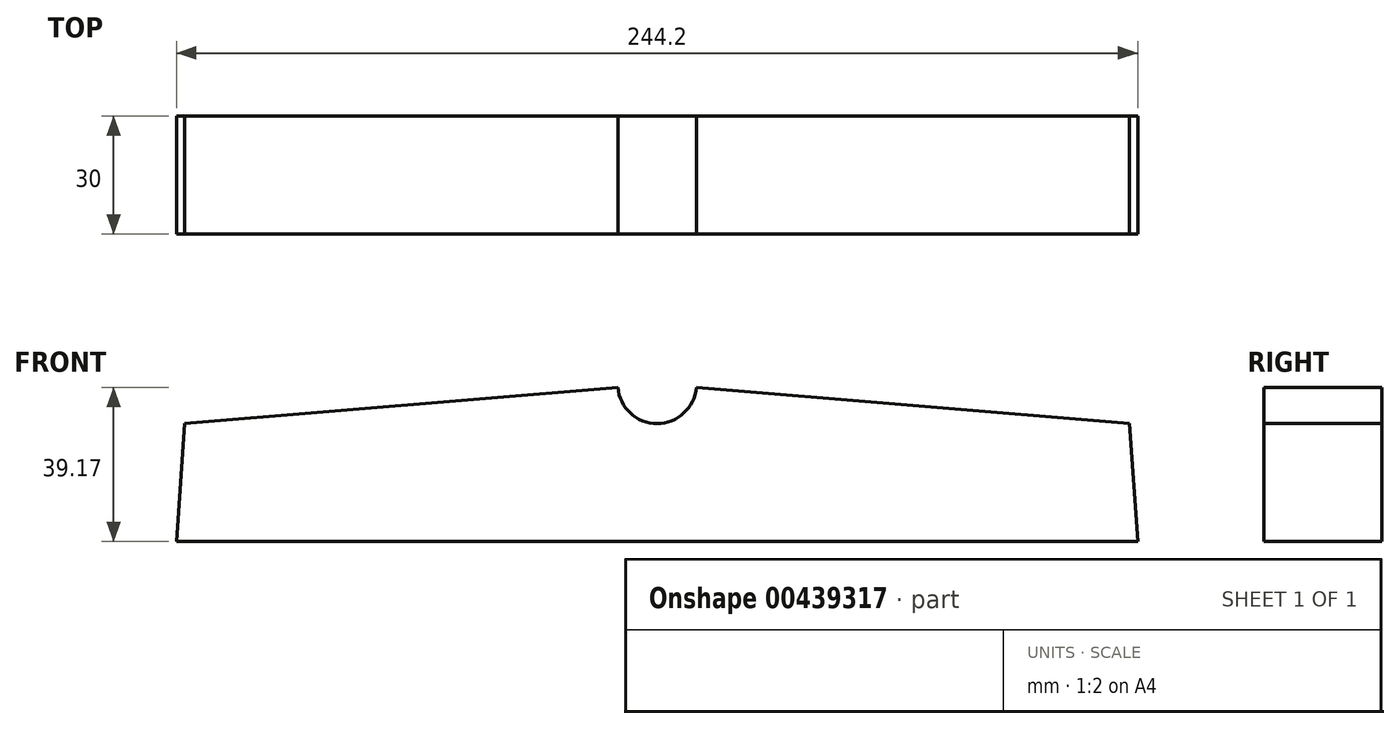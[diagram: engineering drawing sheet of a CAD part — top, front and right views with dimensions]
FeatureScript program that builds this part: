
annotation { "Feature Type Name" : "Feature", "Feature Type Description" : "" }
export const myFeature = defineFeature(function(context is Context, id is Id, definition is map)
    precondition{}
    {
        {
            var Q0;
            Q0=qCreatedBy(makeId("Front.planeOp"),FACE);
            var sketch = newSketch(context, id + "F0", { "sketchPlane" : qUnion([Q0])});
            skLineSegment(sketch, "E0", {"start": v(0, 0) * mm, "end": v(240, 0) * mm});
            skLineSegment(sketch, "E1", {"start": v(0, 0) * mm, "end": v(120, 10) * mm});
            skLineSegment(sketch, "E2", {"start": v(120, 10) * mm, "end": v(240, 0) * mm});
            skLineSegment(sketch, "E3", {"start": v(0, 0) * mm, "end": v(-2.1, -30) * mm});
            skLineSegment(sketch, "E4", {"start": v(-2.1, -30) * mm, "end": v(120, -30) * mm});
            skLineSegment(sketch, "E5.MirrorCS", {"start": v(242.1, -30) * mm, "end": v(120, -30) * mm});
            skLineSegment(sketch, "E6.MirrorCS", {"start": v(240, 0) * mm, "end": v(242.1, -30) * mm});
            skSolve(sketch);
        }
        {
            var Q0;
            Q0 = qSketchRegion(id + "F0", true);
            extrude(context, id + "F1", {"entities" : qUnion([Q0]), "depth" : 30 * mm});
        }
        {
            var Q0;
            Q0=makeQuery(id+"F1.opExtrude","CAP_FACE",FACE,{"disambiguationData":[OSD([sQuery(id+"F0.wireOp",EDGE,"E1"),sQuery(id+"F0.wireOp",EDGE,"E2"),sQuery(id+"F0.wireOp",EDGE,"E3"),sQuery(id+"F0.wireOp",EDGE,"E4"),sQuery(id+"F0.wireOp",EDGE,"E5.MirrorCS"),sQuery(id+"F0.wireOp",EDGE,"E6.MirrorCS")])],"isStart":false});
            var sketch = newSketch(context, id + "F2", { "sketchPlane" : qUnion([Q0])});
            skCircle(sketch, "E7", {"center": v(120, 10) * mm, "radius": 10 * mm});
            skSolve(sketch);
        }
        {
            var Q0;
            Q0 = qSketchRegion(id + "F2", true);
            extrude(context, id + "F3", {"entities" : qUnion([Q0]), "operationType" : NewBodyOperationType.REMOVE, "oppositeDirection" : true, "depth" : 30 * mm});
        }
    });
